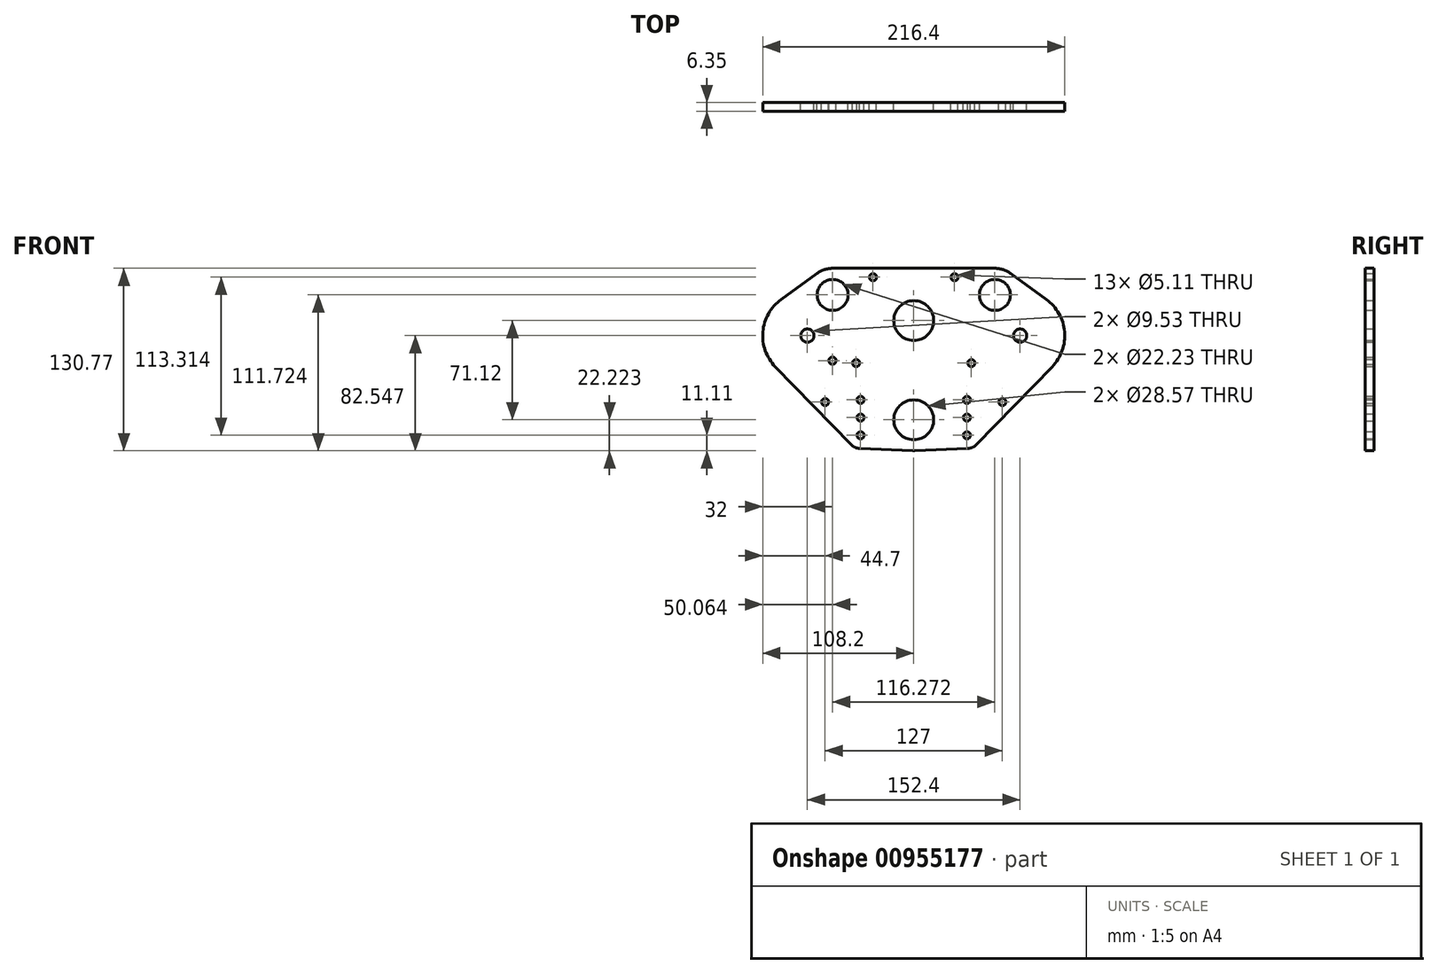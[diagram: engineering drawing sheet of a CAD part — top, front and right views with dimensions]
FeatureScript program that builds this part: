
annotation { "Feature Type Name" : "Feature", "Feature Type Description" : "" }
export const myFeature = defineFeature(function(context is Context, id is Id, definition is map)
    precondition{}
    {
        {
            var Q0;
            Q0=qCreatedBy(makeId("Front.planeOp"),FACE);
            var sketch = newSketch(context, id + "F0", { "sketchPlane" : qUnion([Q0])});
            skCircle(sketch, "E0", {"center": v(-76.2, 58.74) * mm, "radius": 32 * mm, "construction": true});
            skCircle(sketch, "E1", {"center": v(76.2, 58.74) * mm, "radius": 32 * mm, "construction": true});
            skLineSegment(sketch, "E2", {"start": v(-76.2, 58.74) * mm, "end": v(76.2, 58.74) * mm, "construction": true});
            skLineSegment(sketch, "E3", {"start": v(0, 58.74) * mm, "end": v(0, 0) * mm, "construction": true});
            skCircle(sketch, "E4", {"center": v(-76.2, 58.74) * mm, "radius": 7.63 * mm, "construction": true});
            skCircle(sketch, "E5", {"center": v(76.2, 58.74) * mm, "radius": 7.63 * mm, "construction": true});
            skLineSegment(sketch, "E6.bottom", {"start": v(-127, 23.81) * mm, "end": v(127, 23.81) * mm, "construction": true});
            skLineSegment(sketch, "E6.top", {"start": v(-127, -26.99) * mm, "end": v(127, -26.99) * mm, "construction": true});
            skLineSegment(sketch, "E6.left", {"start": v(-127, 23.81) * mm, "end": v(-127, -26.99) * mm, "construction": true});
            skLineSegment(sketch, "E6.right", {"start": v(127, 23.81) * mm, "end": v(127, -26.99) * mm, "construction": true});
            skPoint(sketch, "E6.middle", {"position": v(0, -1.59) * mm});
            skCircle(sketch, "E7", {"center": v(0, 0) * mm, "radius": 50.8 * mm, "construction": true});
            skCircle(sketch, "E8", {"center": v(-58.14, 87.91) * mm, "radius": 26.68 * mm, "construction": true});
            skCircle(sketch, "E9", {"center": v(58.14, 87.91) * mm, "radius": 26.68 * mm, "construction": true});
            skCircle(sketch, "E10", {"center": v(0, 69.53) * mm, "radius": 34.3 * mm, "construction": true});
            skCircle(sketch, "E11", {"center": v(0, 69.53) * mm, "radius": 25.4 * mm, "construction": true});
            skCircle(sketch, "E12", {"center": v(0, 69.53) * mm, "radius": 38.1 * mm, "construction": true});
            skCircle(sketch, "E13", {"center": v(0, -1.59) * mm, "radius": 33.02 * mm, "construction": true});
            skCircle(sketch, "E14", {"center": v(0, -1.59) * mm, "radius": 45.72 * mm, "construction": true});
            skCircle(sketch, "E15", {"center": v(-76.2, 58.74) * mm, "radius": 4.76 * mm});
            skCircle(sketch, "E16", {"center": v(76.2, 58.74) * mm, "radius": 4.76 * mm});
            skCircle(sketch, "E17", {"center": v(-58.14, 87.91) * mm, "radius": 11.11 * mm});
            skCircle(sketch, "E18", {"center": v(58.14, 87.91) * mm, "radius": 11.11 * mm});
            skCircle(sketch, "E19", {"center": v(0, 69.53) * mm, "radius": 14.29 * mm});
            skCircle(sketch, "E20", {"center": v(0, -1.59) * mm, "radius": 14.29 * mm});
            skCircle(sketch, "E21", {"center": v(-38.1, 12.7) * mm, "radius": 9.53 * mm, "construction": true});
            skCircle(sketch, "E22", {"center": v(-38.1, -12.7) * mm, "radius": 9.53 * mm, "construction": true});
            skCircle(sketch, "E23", {"center": v(38.1, -12.7) * mm, "radius": 9.53 * mm, "construction": true});
            skCircle(sketch, "E24", {"center": v(38.1, 12.7) * mm, "radius": 9.53 * mm, "construction": true});
            skCircle(sketch, "E25", {"center": v(38.1, 0) * mm, "radius": 9.53 * mm, "construction": true});
            skCircle(sketch, "E26", {"center": v(-38.1, 0) * mm, "radius": 9.53 * mm, "construction": true});
            skCircle(sketch, "E27", {"center": v(38.1, -12.7) * mm, "radius": 2.55 * mm});
            skCircle(sketch, "E28", {"center": v(38.1, 0) * mm, "radius": 2.55 * mm});
            skCircle(sketch, "E29", {"center": v(38.1, 12.7) * mm, "radius": 2.55 * mm});
            skCircle(sketch, "E30", {"center": v(-38.1, 12.7) * mm, "radius": 2.55 * mm});
            skCircle(sketch, "E31", {"center": v(-38.1, 0) * mm, "radius": 2.55 * mm});
            skCircle(sketch, "E32", {"center": v(-38.1, -12.7) * mm, "radius": 2.55 * mm});
            skLineSegment(sketch, "E33", {"start": v(-44.93, -19.34) * mm, "end": v(-99.15, 36.43) * mm});
            skArc(sketch, "E34", {"start": v(-44.93, -19.34) * mm, "mid": v(-42, -21.4) * mm, "end": v(-38.5, -22.22) * mm});
            skArc(sketch, "E35", {"start": v(38.5, -22.22) * mm, "mid": v(42, -21.4) * mm, "end": v(44.93, -19.34) * mm});
            skLineSegment(sketch, "E36", {"start": v(44.93, -19.34) * mm, "end": v(99.15, 36.43) * mm});
            skCircle(sketch, "E37", {"center": v(58.14, 87.91) * mm, "radius": 19.05 * mm, "construction": true});
            skCircle(sketch, "E38", {"center": v(-58.14, 87.91) * mm, "radius": 19.05 * mm, "construction": true});
            skArc(sketch, "E39", {"start": v(99.15, 36.43) * mm, "mid": v(108.09, 61.46) * mm, "end": v(95.04, 84.61) * mm});
            skArc(sketch, "E40", {"start": v(-95.04, 84.61) * mm, "mid": v(-108.09, 61.46) * mm, "end": v(-99.15, 36.43) * mm});
            skLineSegment(sketch, "E41", {"start": v(-58.24, 40.78) * mm, "end": v(-76.2, 58.74) * mm, "construction": true});
            skLineSegment(sketch, "E42", {"start": v(-76.2, 58.74) * mm, "end": v(-94.16, 76.7) * mm, "construction": true});
            skCircle(sketch, "E43", {"center": v(-94.16, 76.7) * mm, "radius": 2.55 * mm, "construction": true});
            skCircle(sketch, "E44", {"center": v(-58.24, 40.78) * mm, "radius": 2.55 * mm, "construction": true});
            skCircle(sketch, "E45.MirrorC", {"center": v(-58.24, 40.78) * mm, "radius": 2.55 * mm});
            skCircle(sketch, "E46.MirrorC", {"center": v(58.24, 40.78) * mm, "radius": 2.55 * mm, "construction": true});
            skLineSegment(sketch, "E47.MirrorCS", {"start": v(58.24, 40.78) * mm, "end": v(76.2, 58.74) * mm, "construction": true});
            skLineSegment(sketch, "E48.MirrorCS", {"start": v(76.2, 58.74) * mm, "end": v(94.16, 76.7) * mm, "construction": true});
            skCircle(sketch, "E49.MirrorC", {"center": v(94.16, 76.7) * mm, "radius": 2.55 * mm, "construction": true});
            skLineSegment(sketch, "E50", {"start": v(95.04, 84.61) * mm, "end": v(69.35, 103.31) * mm});
            skLineSegment(sketch, "E51", {"start": v(-95.04, 84.61) * mm, "end": v(-69.35, 103.31) * mm});
            skLineSegment(sketch, "E52", {"start": v(-58.14, 106.96) * mm, "end": v(58.14, 106.96) * mm});
            skArc(sketch, "E53", {"start": v(-69.35, 103.31) * mm, "mid": v(-64.03, 106.03) * mm, "end": v(-58.14, 106.96) * mm});
            skArc(sketch, "E54", {"start": v(58.14, 106.96) * mm, "mid": v(64.03, 106.03) * mm, "end": v(69.35, 103.31) * mm});
            skCircle(sketch, "E55", {"center": v(0, -1.59) * mm, "radius": 22.23 * mm, "construction": true});
            skLineSegment(sketch, "E56", {"start": v(38.5, -22.22) * mm, "end": v(0.93, -23.8) * mm});
            skLineSegment(sketch, "E57", {"start": v(-38.5, -22.22) * mm, "end": v(-0.93, -23.8) * mm});
            skArc(sketch, "E58", {"start": v(-0.93, -23.8) * mm, "mid": v(0, -23.81) * mm, "end": v(0.93, -23.8) * mm});
            skLineSegment(sketch, "E59.bottom", {"start": v(-38.1, -12.7) * mm, "end": v(38.1, -12.7) * mm, "construction": true});
            skLineSegment(sketch, "E59.top", {"start": v(-38.1, 12.7) * mm, "end": v(38.1, 12.7) * mm, "construction": true});
            skLineSegment(sketch, "E59.left", {"start": v(-38.1, -12.7) * mm, "end": v(-38.1, 12.7) * mm, "construction": true});
            skLineSegment(sketch, "E59.right", {"start": v(38.1, -12.7) * mm, "end": v(38.1, 12.7) * mm, "construction": true});
            skCircle(sketch, "E60", {"center": v(-29.21, 100.61) * mm, "radius": 6.35 * mm, "construction": true});
            skCircle(sketch, "E61", {"center": v(-29.21, 100.61) * mm, "radius": 2.55 * mm});
            skCircle(sketch, "E62.MirrorC", {"center": v(29.2, 100.61) * mm, "radius": 6.35 * mm, "construction": true});
            skCircle(sketch, "E63.MirrorC", {"center": v(29.2, 100.61) * mm, "radius": 2.55 * mm});
            skCircle(sketch, "E64", {"center": v(-63.5, 11.15) * mm, "radius": 7.94 * mm, "construction": true});
            skCircle(sketch, "E65", {"center": v(-63.5, 11.15) * mm, "radius": 2.55 * mm});
            skCircle(sketch, "E66.MirrorC", {"center": v(63.5, 11.15) * mm, "radius": 7.94 * mm, "construction": true});
            skCircle(sketch, "E67.MirrorC", {"center": v(63.5, 11.15) * mm, "radius": 2.55 * mm});
            skCircle(sketch, "E68", {"center": v(-41.28, 39.05) * mm, "radius": 6.35 * mm, "construction": true});
            skCircle(sketch, "E69", {"center": v(41.28, 39.05) * mm, "radius": 6.35 * mm, "construction": true});
            skCircle(sketch, "E70", {"center": v(41.28, 39.05) * mm, "radius": 2.55 * mm});
            skCircle(sketch, "E71", {"center": v(-41.28, 39.05) * mm, "radius": 2.55 * mm});
            skLineSegment(sketch, "E72", {"start": v(41.28, 39.05) * mm, "end": v(-41.28, 39.05) * mm, "construction": true});
            skLineSegment(sketch, "E73", {"start": v(0, 39.05) * mm, "end": v(0, 69.53) * mm, "construction": true});
            skSolve(sketch);
        }
        {
            var Q0;
            Q0=qSketchRegion(id+"F0",true);
            extrude(context, id + "F1", {"entities" : qUnion([Q0]), "depth" : 6.35 * mm, "offsetDistance" : 25.4 * mm});
        }
    });
